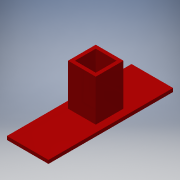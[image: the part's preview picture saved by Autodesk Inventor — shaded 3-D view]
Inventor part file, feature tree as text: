
AUTODESK INVENTOR PART (.ipt)
format: ipt  version: 2016 (Build 200138000, 138)  size: 113,664 bytes
history: native  units: in
note: dims shown in document units (in); Inventor stores cm internally (conversion verified against a paired STEP export)
features: extrude x3, sketch x2
ambient origin geometry x8: Origin, YZ Plane, XZ Plane, XY Plane, X Axis, Y Axis, Z Axis, Center Point
bodies: Solid1 (feature_tree)
feature tree (5):
  extrude  "Extrusion1"  Depth=4.5in
  sketch  "Sketch3"  dims[d2=0.125in d3=0.0in d8=1.0in d9=1.0in d10=0.25in d12=0.125in d13=1.5in d14=0.0in d15=0.2in d16=0.5in d17=0.5in d20=0.125in d21=0.0in d23=1.458in]
  extrude  "Extrusion3"  Depth=1.0in
  extrude  "Extrusion5"  Depth=1.0in
  sketch  "Sketch1"  dims[d0=1.5in d1=4.5in]
